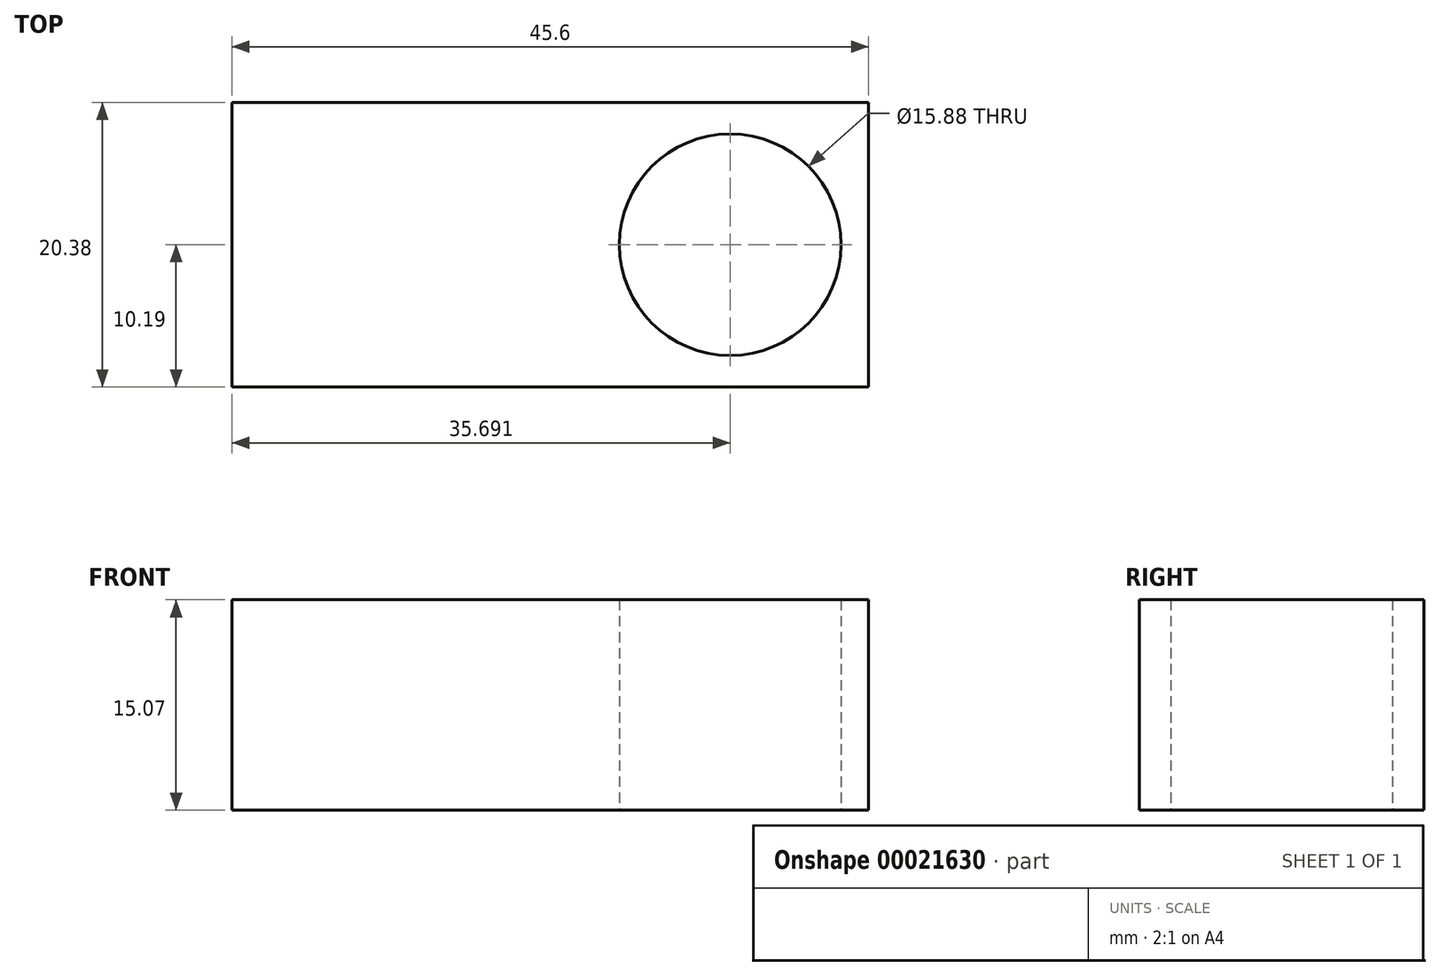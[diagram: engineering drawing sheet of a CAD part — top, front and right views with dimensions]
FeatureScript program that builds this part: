
annotation { "Feature Type Name" : "Feature", "Feature Type Description" : "" }
export const myFeature = defineFeature(function(context is Context, id is Id, definition is map)
    precondition{}
    {
        {
            var Q0;
            Q0=qCreatedBy(makeId("Top.planeOp"),FACE);
            var sketch = newSketch(context, id + "F0", { "sketchPlane" : qUnion([Q0])});
            skCircle(sketch, "E0", {"center": v(-12.9, 0) * mm, "radius": 7.94 * mm});
            skLineSegment(sketch, "E1", {"start": v(0, 0) * mm, "end": v(0, 20.66) * mm, "construction": true});
            skCircle(sketch, "E2.MirrorC", {"center": v(12.9, 0) * mm, "radius": 7.94 * mm});
            skLineSegment(sketch, "E3", {"start": v(-22.8, 10.19) * mm, "end": v(-22.8, -10.19) * mm});
            skLineSegment(sketch, "E4.MirrorCS", {"start": v(22.8, 10.19) * mm, "end": v(22.8, -10.19) * mm});
            skLineSegment(sketch, "E5", {"start": v(-22.8, 10.19) * mm, "end": v(22.8, 10.19) * mm});
            skLineSegment(sketch, "E6", {"start": v(-22.8, -10.19) * mm, "end": v(22.8, -10.19) * mm});
            skSolve(sketch);
        }
        {
            var Q0;
            Q0=makeQuery(id+"F0.imprint","IMPRINT",FACE,{"disambiguationData":[TD([[makeQuery(id+"F0.imprint","IMPRINT",EDGE,{"derivedFrom":sQuery(id+"F0.wireOp",EDGE,"E2.MirrorC")}),-1.0]])]});
            var Q1;
            Q1=makeQuery(id+"F0.imprint","IMPRINT",FACE,{"disambiguationData":[TD([[makeQuery(id+"F0.imprint","IMPRINT",EDGE,{"derivedFrom":sQuery(id+"F0.wireOp",EDGE,"E0")}),1.0]])]});
            var Q2;
            Q2=makeQuery(id+"F0.imprint","IMPRINT",FACE,{"disambiguationData":[TD([[makeQuery(id+"F0.imprint","IMPRINT",EDGE,{"derivedFrom":sQuery(id+"F0.wireOp",EDGE,"E0")}),-1.0]])]});
            extrude(context, id + "F1", {"entities" : qUnion([Q0, Q1, Q2]), "depth" : 3.23 * mm, "offsetDistance" : 25.4 * mm});
        }
        {
            var Q0;
            Q0=makeQuery(id+"F0.imprint","IMPRINT",FACE,{"disambiguationData":[TD([[makeQuery(id+"F0.imprint","IMPRINT",EDGE,{"derivedFrom":sQuery(id+"F0.wireOp",EDGE,"E0")}),1.0]])]});
            var Q1;
            Q1=makeQuery(id+"F0.imprint","IMPRINT",FACE,{"disambiguationData":[TD([[makeQuery(id+"F0.imprint","IMPRINT",EDGE,{"derivedFrom":sQuery(id+"F0.wireOp",EDGE,"E2.MirrorC")}),-1.0]])]});
            extrude(context, id + "F2", {"entities" : qUnion([Q0, Q1]), "operationType" : NewBodyOperationType.ADD, "oppositeDirection" : true, "depth" : 11.84 * mm, "offsetDistance" : 25.4 * mm});
        }
    });
